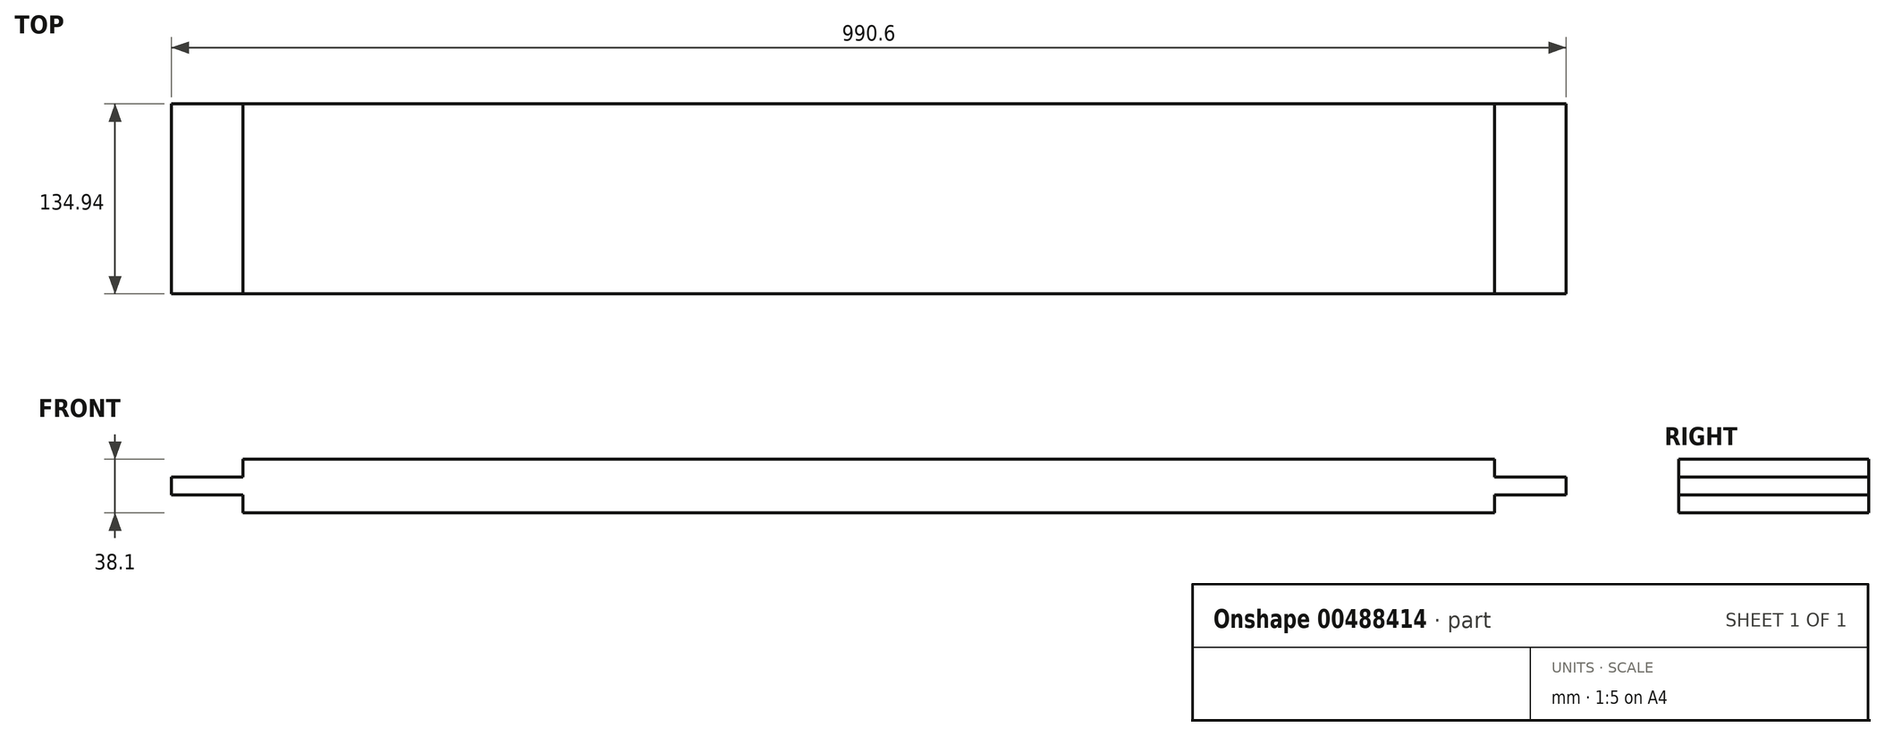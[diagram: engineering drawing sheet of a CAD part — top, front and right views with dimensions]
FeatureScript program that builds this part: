
annotation { "Feature Type Name" : "Feature", "Feature Type Description" : "" }
export const myFeature = defineFeature(function(context is Context, id is Id, definition is map)
    precondition{}
    {
        {
            var Q0;
            Q0=qCreatedBy(makeId("Top.planeOp"),FACE);
            var sketch = newSketch(context, id + "F0", { "sketchPlane" : qUnion([Q0])});
            skLineSegment(sketch, "E0.bottom", {"start": v(495.3, 67.47) * mm, "end": v(-495.3, 67.47) * mm});
            skLineSegment(sketch, "E0.top", {"start": v(495.3, -67.47) * mm, "end": v(-495.3, -67.47) * mm});
            skLineSegment(sketch, "E0.left", {"start": v(495.3, 67.47) * mm, "end": v(495.3, -67.47) * mm});
            skLineSegment(sketch, "E0.right", {"start": v(-495.3, 67.47) * mm, "end": v(-495.3, -67.47) * mm});
            skPoint(sketch, "E0.middle", {"position": v(0, 0) * mm});
            skSolve(sketch);
        }
        {
            var Q0;
            Q0 = qSketchRegion(id + "F0", true);
            extrude(context, id + "F1", {"entities" : qUnion([Q0]), "flatOperationType" : FlatOperationType.REMOVE, "offsetDistance" : 25.4 * mm, "depth" : 38.1 * mm, "domain" : OperationDomain.MODEL, "symmetric" : true});
        }
        {
            var Q0;
            Q0=makeQuery(id+"F1.opExtrude","SWEPT_FACE",FACE,{"disambiguationData":[OSD([sQuery(id+"F0.wireOp",EDGE,"E0.top")])]});
            var sketch = newSketch(context, id + "F2", { "sketchPlane" : qUnion([Q0])});
            skLineSegment(sketch, "E1", {"start": v(-444.5, 19.05) * mm, "end": v(-444.5, 6.35) * mm});
            skLineSegment(sketch, "E2", {"start": v(-495.3, 6.35) * mm, "end": v(-444.5, 6.35) * mm});
            skLineSegment(sketch, "E3", {"start": v(-444.5, -6.35) * mm, "end": v(-495.3, -6.35) * mm});
            skLineSegment(sketch, "E4.0", {"start": v(-495.3, 19.05) * mm, "end": v(-495.3, 6.35) * mm});
            skLineSegment(sketch, "E5.trimOffspring", {"start": v(-444.5, -6.35) * mm, "end": v(-444.5, -19.05) * mm});
            skLineSegment(sketch, "E6.trimOffspring", {"start": v(-495.3, -6.35) * mm, "end": v(-495.3, -19.05) * mm});
            skLineSegment(sketch, "E7.0", {"start": v(495.3, 19.05) * mm, "end": v(444.5, 19.05) * mm});
            skLineSegment(sketch, "E7.1", {"start": v(495.3, -19.05) * mm, "end": v(444.5, -19.05) * mm});
            skLineSegment(sketch, "E8.MirrorCS", {"start": v(444.5, -6.35) * mm, "end": v(444.5, -19.05) * mm});
            skLineSegment(sketch, "E9.MirrorCS", {"start": v(444.5, -6.35) * mm, "end": v(495.3, -6.35) * mm});
            skLineSegment(sketch, "E10.MirrorCS", {"start": v(495.3, 6.35) * mm, "end": v(444.5, 6.35) * mm});
            skLineSegment(sketch, "E11.MirrorCS", {"start": v(444.5, 19.05) * mm, "end": v(444.5, 6.35) * mm});
            skLineSegment(sketch, "E12.trimOffspring", {"start": v(-444.5, 19.05) * mm, "end": v(-495.3, 19.05) * mm});
            skLineSegment(sketch, "E13.trimOffspring", {"start": v(-444.5, -19.05) * mm, "end": v(-495.3, -19.05) * mm});
            skLineSegment(sketch, "E14.0", {"start": v(495.3, 19.05) * mm, "end": v(495.3, 6.35) * mm});
            skLineSegment(sketch, "E15.trimOffspring", {"start": v(495.3, -6.35) * mm, "end": v(495.3, -19.05) * mm});
            skSolve(sketch);
        }
        {
            var Q0;
            Q0 = qSketchRegion(id + "F2", true);
            var Q1;
            Q1=makeQuery(id+"F1.opExtrude","SWEPT_FACE",FACE,{"disambiguationData":[OSD([sQuery(id+"F0.wireOp",EDGE,"E0.bottom")])]});
            extrude(context, id + "F3", {"entities" : qUnion([Q0]), "operationType" : NewBodyOperationType.REMOVE, "endBound" : BoundingType.UP_TO_SURFACE, "oppositeDirection" : true, "endBoundEntityFace" : qUnion([Q1]), "depth" : 25.4 * mm});
        }
    });
